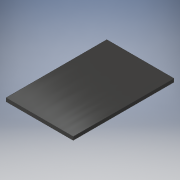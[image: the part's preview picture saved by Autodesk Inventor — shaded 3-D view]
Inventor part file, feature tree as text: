
AUTODESK INVENTOR PART (.ipt)
format: ipt  version: 2019 (Build 230136000, 136)  size: 96,256 bytes
history: native  units: in
note: dims shown in document units (in); Inventor stores cm internally (conversion verified against a paired STEP export)
features: extrude x1, sketch x1
ambient origin geometry x8: Origin, YZ Plane, XZ Plane, XY Plane, X Axis, Y Axis, Z Axis, Center Point
bodies: Solid1 (feature_tree)
feature tree (2):
  extrude  "Extrusion1"  Depth=5.9055in
  sketch  "Sketch1"  dims[d0=3.937in d1=5.9055in d2=2.9528in d3=1.9685in d4=0.1969in d5=0.0in]
